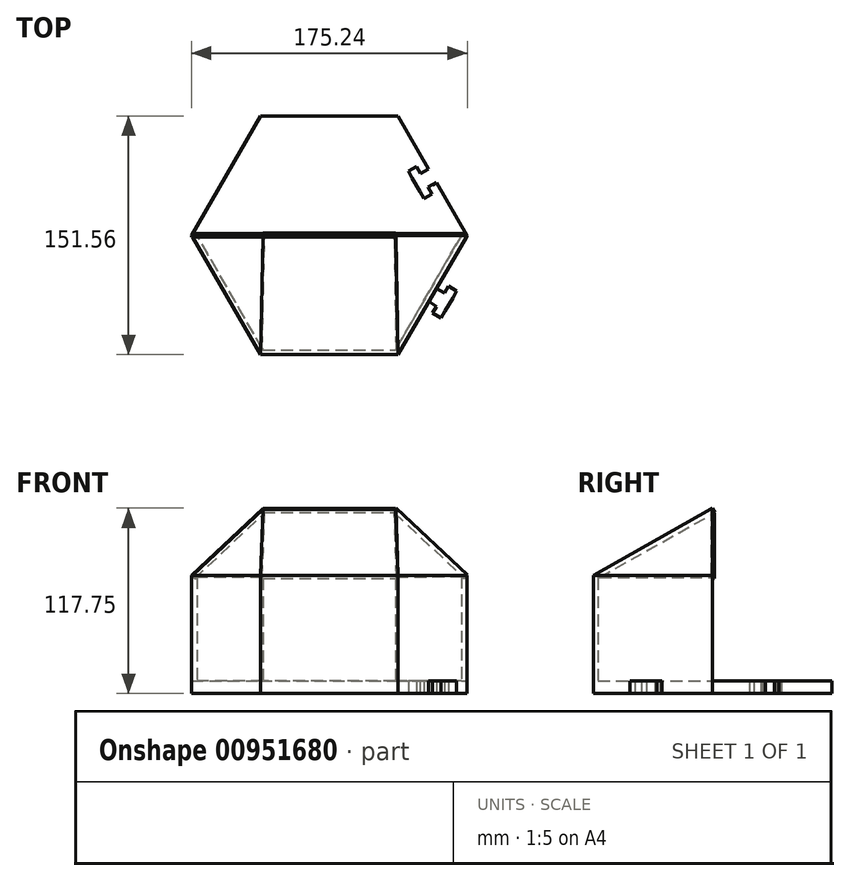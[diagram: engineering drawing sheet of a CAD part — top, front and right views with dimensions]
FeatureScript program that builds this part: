
annotation { "Feature Type Name" : "Feature", "Feature Type Description" : "" }
export const myFeature = defineFeature(function(context is Context, id is Id, definition is map)
    precondition{}
    {
        {
            var Q0;
            Q0=qCreatedBy(makeId("Top.planeOp"),FACE);
            var sketch = newSketch(context, id + "F0", { "sketchPlane" : qUnion([Q0])});
            skCircle(sketch, "E0.cCircle", {"center": v(0, 0) * mm, "radius": 75.78 * mm, "construction": true});
            skLineSegment(sketch, "E0.0", {"start": v(-43.75, 75.78) * mm, "end": v(43.75, 75.78) * mm});
            skLineSegment(sketch, "E0.1", {"start": v(43.75, 75.78) * mm, "end": v(87.5, 0) * mm});
            skLineSegment(sketch, "E0.2", {"start": v(87.5, 0) * mm, "end": v(43.75, -75.78) * mm});
            skLineSegment(sketch, "E0.3", {"start": v(43.75, -75.78) * mm, "end": v(-43.75, -75.78) * mm});
            skLineSegment(sketch, "E0.4", {"start": v(-43.75, -75.78) * mm, "end": v(-87.5, 0) * mm});
            skLineSegment(sketch, "E0.5", {"start": v(-87.5, 0) * mm, "end": v(-43.75, 75.78) * mm});
            skPoint(sketch, "E0.0.midPoint", {"position": v(0, 75.78) * mm});
            skLineSegment(sketch, "E1.0", {"start": v(-84.04, 0) * mm, "end": v(-42.02, 72.78) * mm});
            skLineSegment(sketch, "E1.1", {"start": v(42.02, 72.78) * mm, "end": v(84.04, 0) * mm});
            skLineSegment(sketch, "E1.2", {"start": v(84.04, 0) * mm, "end": v(42.02, -72.78) * mm});
            skLineSegment(sketch, "E1.3", {"start": v(-42.02, 72.78) * mm, "end": v(42.02, 72.78) * mm});
            skLineSegment(sketch, "E1.4", {"start": v(42.02, -72.78) * mm, "end": v(-42.02, -72.78) * mm});
            skLineSegment(sketch, "E1.5", {"start": v(-42.02, -72.78) * mm, "end": v(-84.04, 0) * mm});
            skLineSegment(sketch, "E2", {"start": v(-87.5, 0) * mm, "end": v(-84.04, 0) * mm});
            skLineSegment(sketch, "E3", {"start": v(84.04, 0) * mm, "end": v(87.5, 0) * mm});
            skLineSegment(sketch, "E4", {"start": v(0, 0) * mm, "end": v(0, 72.78) * mm, "construction": true});
            skLineSegment(sketch, "E5", {"start": v(0, 0) * mm, "end": v(42.02, 72.78) * mm, "construction": true});
            skLineSegment(sketch, "E6", {"start": v(0, 0) * mm, "end": v(-42.02, 72.78) * mm, "construction": true});
            skLineSegment(sketch, "E7", {"start": v(0, 36.39) * mm, "end": v(0, 72.78) * mm, "construction": true});
            skLineSegment(sketch, "E8.bottom", {"start": v(25, 48.33) * mm, "end": v(-25, 48.33) * mm});
            skLineSegment(sketch, "E8.top", {"start": v(25, 60.83) * mm, "end": v(-25, 60.83) * mm});
            skLineSegment(sketch, "E8.left", {"start": v(25, 48.33) * mm, "end": v(25, 60.83) * mm});
            skLineSegment(sketch, "E8.right", {"start": v(-25, 48.33) * mm, "end": v(-25, 60.83) * mm});
            skPoint(sketch, "E8.middle", {"position": v(0, 54.58) * mm});
            skLineSegment(sketch, "E9", {"start": v(-55.16, 32) * mm, "end": v(-52.71, 36.37) * mm, "construction": true});
            skLineSegment(sketch, "E10", {"start": v(-65.63, 37.89) * mm, "end": v(-68.13, 33.56) * mm});
            skLineSegment(sketch, "E11.MirrorCS", {"start": v(55.16, 32) * mm, "end": v(57.62, 27.65) * mm});
            skLineSegment(sketch, "E12.MirrorCS", {"start": v(55.16, 32) * mm, "end": v(52.71, 36.37) * mm});
            skLineSegment(sketch, "E13.MirrorCS", {"start": v(57.62, 27.65) * mm, "end": v(68.13, 33.56) * mm});
            skLineSegment(sketch, "E14.MirrorCS", {"start": v(87.5, 0) * mm, "end": v(43.75, 75.78) * mm});
            skLineSegment(sketch, "E15.MirrorCS", {"start": v(52.71, 36.37) * mm, "end": v(63.12, 42.22) * mm});
            skLineSegment(sketch, "E16.MirrorCS", {"start": v(57.97, 39.32) * mm, "end": v(55.52, 43.68) * mm});
            skLineSegment(sketch, "E17.MirrorCS", {"start": v(55.52, 43.68) * mm, "end": v(50.26, 40.72) * mm});
            skLineSegment(sketch, "E18.MirrorCS", {"start": v(52.71, 36.37) * mm, "end": v(50.26, 40.72) * mm});
            skLineSegment(sketch, "E19.MirrorCS", {"start": v(57.62, 27.65) * mm, "end": v(60.07, 23.3) * mm});
            skLineSegment(sketch, "E20.MirrorCS", {"start": v(62.87, 30.6) * mm, "end": v(65.32, 26.25) * mm});
            skLineSegment(sketch, "E21.MirrorCS", {"start": v(65.32, 26.25) * mm, "end": v(60.07, 23.3) * mm});
            skPoint(sketch, "E22.endSnap0", {"position": v(-68.26, -45.15) * mm});
            skLineSegment(sketch, "E23.MirrorCS", {"start": v(68.26, -45.15) * mm, "end": v(65.74, -49.4) * mm});
            skLineSegment(sketch, "E24.MirrorCS", {"start": v(65.74, -49.4) * mm, "end": v(70.88, -52.4) * mm});
            skLineSegment(sketch, "E25.MirrorCS", {"start": v(73.4, -48.2) * mm, "end": v(70.88, -52.4) * mm});
            skLineSegment(sketch, "E26.MirrorCS", {"start": v(73.4, -48.2) * mm, "end": v(63.12, -42.1) * mm});
            skLineSegment(sketch, "E27.MirrorCS", {"start": v(78.45, -39.68) * mm, "end": v(73.4, -48.2) * mm});
            skLineSegment(sketch, "E28.MirrorCS", {"start": v(78.45, -39.68) * mm, "end": v(68.12, -33.56) * mm});
            skLineSegment(sketch, "E29.MirrorCS", {"start": v(73.33, -36.65) * mm, "end": v(75.88, -32.34) * mm});
            skLineSegment(sketch, "E30.MirrorCS", {"start": v(75.88, -32.34) * mm, "end": v(80.95, -35.46) * mm});
            skLineSegment(sketch, "E31.MirrorCS", {"start": v(78.45, -39.68) * mm, "end": v(81, -35.38) * mm});
            skLineSegment(sketch, "E32", {"start": v(68.13, 33.56) * mm, "end": v(65.53, 32.06) * mm});
            skSolve(sketch);
        }
        {
            var Q0;
            Q0=makeQuery(id+"F0.imprint","IMPRINT",FACE,{"disambiguationData":[TD([[makeQuery(id+"F0.imprint","IMPRINT",EDGE,{"derivedFrom":sQuery(id+"F0.wireOp",EDGE,"E1.0")}),-1.0]])]});
            extrude(context, id + "F1", {"entities" : qUnion([Q0]), "depth" : 8 * mm, "offsetDistance" : 25 * mm});
        }
        {
            var Q0;
            Q0=makeQuery(id+"F0.imprint","IMPRINT",FACE,{"disambiguationData":[TD([[makeQuery(id+"F0.imprint","IMPRINT",EDGE,{"derivedFrom":sQuery(id+"F0.wireOp",EDGE,"E0.2")}),-1.0]])]});
            extrude(context, id + "F2", {"entities" : qUnion([Q0]), "operationType" : NewBodyOperationType.ADD, "depth" : 75 * mm, "offsetDistance" : 25 * mm});
        }
        {
            var Q0;
            Q0=qCreatedBy(makeId("Front.planeOp"),FACE);
            var sketch = newSketch(context, id + "F3", { "sketchPlane" : qUnion([Q0])});
            skLineSegment(sketch, "E33", {"start": v(0, 0) * mm, "end": v(0, 144.27) * mm, "construction": true});
            skLineSegment(sketch, "E34", {"start": v(0, 144.27) * mm, "end": v(-94, 144.27) * mm, "construction": true});
            skLineSegment(sketch, "E35", {"start": v(0, 144.27) * mm, "end": v(81.74, 144.27) * mm});
            skLineSegment(sketch, "E36", {"start": v(0, 0) * mm, "end": v(0, 75) * mm, "construction": true});
            skLineSegment(sketch, "E37", {"start": v(0, 75) * mm, "end": v(0, 114.5) * mm, "construction": true});
            skLineSegment(sketch, "E38", {"start": v(0, 75) * mm, "end": v(-87.5, 75) * mm, "construction": true});
            skLineSegment(sketch, "E39", {"start": v(0, 114.5) * mm, "end": v(42.02, 114.5) * mm, "construction": true});
            skLineSegment(sketch, "E40", {"start": v(0, 114.5) * mm, "end": v(-42.02, 114.5) * mm});
            skLineSegment(sketch, "E41", {"start": v(0, 75) * mm, "end": v(-84.04, 75) * mm, "construction": true});
            skLineSegment(sketch, "E42", {"start": v(-42.02, 114.5) * mm, "end": v(-84.04, 75) * mm});
            skLineSegment(sketch, "E43", {"start": v(-42.02, 114.5) * mm, "end": v(-42.02, 117.5) * mm, "construction": true});
            skLineSegment(sketch, "E44", {"start": v(-42.02, 117.5) * mm, "end": v(-87.5, 75) * mm});
            skLineSegment(sketch, "E45", {"start": v(-42.02, 117.5) * mm, "end": v(0, 117.5) * mm});
            skLineSegment(sketch, "E46.MirrorCS", {"start": v(42.02, 117.5) * mm, "end": v(87.5, 75) * mm});
            skLineSegment(sketch, "E47.MirrorCS", {"start": v(42.02, 114.5) * mm, "end": v(84.04, 75) * mm});
            skLineSegment(sketch, "E48.MirrorCS", {"start": v(42.02, 117.5) * mm, "end": v(0, 117.5) * mm});
            skLineSegment(sketch, "E49.MirrorCS", {"start": v(0, 114.5) * mm, "end": v(42.02, 114.5) * mm});
            skLineSegment(sketch, "E50", {"start": v(87.5, 75) * mm, "end": v(84.04, 75) * mm});
            skLineSegment(sketch, "E51", {"start": v(-84.04, 75) * mm, "end": v(-87.5, 75) * mm});
            skSolve(sketch);
        }
        {
            var Q0;
            Q0=makeQuery(id+"F0.imprint","IMPRINT",FACE,{"disambiguationData":[TD([[makeQuery(id+"F0.imprint","IMPRINT",EDGE,{"derivedFrom":sQuery(id+"F0.wireOp",EDGE,"E0.0")}),-1.0]])]});
            extrude(context, id + "F4", {"entities" : qUnion([Q0]), "operationType" : NewBodyOperationType.ADD, "oppositeDirection" : true, "depth" : -8 * mm, "offsetDistance" : 25 * mm});
        }
        {
            var Q0;
            Q0=makeQuery(id+"F2.opExtrude","CAP_EDGE",EDGE,{"disambiguationData":[OSD([sQuery(id+"F0.wireOp",EDGE,"E0.3")])],"isStart":false});
            var Q1;
            Q1=sQuery(id+"F3.wireOp",VERTEX,"E45.end");
            cPlane(context, id + "F5", {"entities" : qUnion([Q0, Q1]), "cplaneType" : CPlaneType.LINE_ANGLE, "offset" : 25 * mm, "angle" : 0 * degree, "width" : 150 * mm, "height" : 150 * mm});
        }
        {
            var Q0;
            Q0=qCreatedBy(id+"F5.planeOp",FACE);
            var sketch = newSketch(context, id + "F6", { "sketchPlane" : qUnion([Q0])});
            skLineSegment(sketch, "E52", {"start": v(0, 29.4) * mm, "end": v(43.75, 29.4) * mm});
            skLineSegment(sketch, "E53", {"start": v(0, 29.4) * mm, "end": v(-43.75, 29.4) * mm});
            skLineSegment(sketch, "E54", {"start": v(-43.75, 29.4) * mm, "end": v(-42.02, -57.48) * mm});
            skLineSegment(sketch, "E55", {"start": v(43.75, 29.4) * mm, "end": v(42.02, -57.48) * mm});
            skLineSegment(sketch, "E56", {"start": v(-42.02, -57.48) * mm, "end": v(42.02, -57.48) * mm});
            skSolve(sketch);
        }
        {
            var Q0;
            Q0=makeQuery(id+"F6.imprint","IMPRINT",FACE,{"disambiguationData":[TD([[makeQuery(id+"F6.imprint","IMPRINT",EDGE,{"derivedFrom":sQuery(id+"F6.wireOp",EDGE,"E52")}),-1.0]])]});
            extrude(context, id + "F7", {"entities" : qUnion([Q0]), "operationType" : NewBodyOperationType.ADD, "depth" : 3 * mm, "offsetDistance" : 25 * mm});
        }
        {
            var Q0;
            Q0=makeQuery(id+"F3.imprint","IMPRINT",FACE,{"disambiguationData":[TD([[makeQuery(id+"F3.imprint","IMPRINT",EDGE,{"derivedFrom":sQuery(id+"F3.wireOp",EDGE,"E40")}),-1.0]])]});
            extrude(context, id + "F8", {"entities" : qUnion([Q0]), "operationType" : NewBodyOperationType.ADD, "depth" : 1 * mm, "offsetDistance" : 25 * mm});
        }
        {
            var Q0;
            Q0=makeQuery(id+"F8.opExtrude","CAP_EDGE",EDGE,{"disambiguationData":[OSD([sQuery(id+"F3.wireOp",EDGE,"E44")])],"isStart":true});
            var Q1;
            Q1=makeQuery(id+"F7.boolean.opBoolean","MERGE",VERTEX,{"derivedFrom":[makeQuery(id+"F2.opExtrude","CAP_VERTEX",VERTEX,{"disambiguationData":[OSD([sQuery(id+"F0.wireOp",EDGE,"E0.3"),sQuery(id+"F0.wireOp",EDGE,"E0.4")])],"isStart":false}),makeQuery(id+"F7.opExtrude","CAP_VERTEX",VERTEX,{"disambiguationData":[OSD([sQuery(id+"F6.wireOp",EDGE,"E53"),sQuery(id+"F6.wireOp",EDGE,"E54")])],"isStart":true})]});
            cPlane(context, id + "F9", {"entities" : qUnion([Q0, Q1]), "cplaneType" : CPlaneType.LINE_ANGLE, "offset" : 25 * mm, "angle" : 0 * degree, "width" : 150 * mm, "height" : 150 * mm});
        }
        {
            var Q0;
            Q0=qCreatedBy(id+"F9.planeOp",FACE);
            var sketch = newSketch(context, id + "F10", { "sketchPlane" : qUnion([Q0])});
            skLineSegment(sketch, "E57", {"start": v(-25.66, 35.61) * mm, "end": v(30.99, -31.08) * mm});
            skLineSegment(sketch, "E58", {"start": v(-25.66, 35.61) * mm, "end": v(33.23, 55.79) * mm});
            skLineSegment(sketch, "E59", {"start": v(33.23, 55.79) * mm, "end": v(30.99, -31.08) * mm});
            skSolve(sketch);
        }
        {
            var Q0;
            Q0=qSketchRegion(id+"F10",true);
            extrude(context, id + "F11", {"entities" : qUnion([Q0]), "operationType" : NewBodyOperationType.ADD, "depth" : -3 * mm, "offsetDistance" : 25 * mm});
        }
        {
            var Q0;
            Q0=makeQuery(id+"F8.opExtrude","CAP_EDGE",EDGE,{"disambiguationData":[OSD([sQuery(id+"F3.wireOp",EDGE,"E46.MirrorCS")])],"isStart":false});
            var Q1;
            Q1=makeQuery(id+"F7.boolean.opBoolean","MERGE",VERTEX,{"derivedFrom":[makeQuery(id+"F2.opExtrude","CAP_VERTEX",VERTEX,{"disambiguationData":[OSD([sQuery(id+"F0.wireOp",EDGE,"E0.2"),sQuery(id+"F0.wireOp",EDGE,"E0.3")])],"isStart":false}),makeQuery(id+"F7.opExtrude","CAP_VERTEX",VERTEX,{"disambiguationData":[OSD([sQuery(id+"F6.wireOp",EDGE,"E52"),sQuery(id+"F6.wireOp",EDGE,"E55")])],"isStart":true})]});
            cPlane(context, id + "F12", {"entities" : qUnion([Q0, Q1]), "cplaneType" : CPlaneType.LINE_ANGLE, "offset" : 25 * mm, "angle" : 0 * degree, "width" : 150 * mm, "height" : 150 * mm});
        }
        {
            var Q0;
            Q0=qCreatedBy(id+"F12.planeOp",FACE);
            var sketch = newSketch(context, id + "F13", { "sketchPlane" : qUnion([Q0])});
            skLineSegment(sketch, "E60", {"start": v(-32.88, -56.36) * mm, "end": v(25.94, -35.98) * mm});
            skLineSegment(sketch, "E61", {"start": v(25.94, -35.98) * mm, "end": v(-30.94, 30.51) * mm});
            skLineSegment(sketch, "E62", {"start": v(-30.94, 30.51) * mm, "end": v(-32.88, -56.36) * mm});
            skSolve(sketch);
        }
        {
            var Q0;
            Q0=qSketchRegion(id+"F13",true);
            extrude(context, id + "F14", {"entities" : qUnion([Q0]), "operationType" : NewBodyOperationType.ADD, "depth" : 3 * mm, "offsetDistance" : 25 * mm});
        }
        {
            var Q0;
            Q0=makeQuery(id+"F0.imprint","IMPRINT",FACE,{"disambiguationData":[TD([[makeQuery(id+"F0.imprint","IMPRINT",EDGE,{"derivedFrom":sQuery(id+"F0.wireOp",EDGE,"E8.bottom")}),-1.0]])]});
            extrude(context, id + "F15", {"entities" : qUnion([Q0]), "operationType" : NewBodyOperationType.ADD, "depth" : 8 * mm, "offsetDistance" : 25 * mm});
        }
        {
            var Q0;
            {var subQ5=sQuery(id+"F0.wireOp",EDGE,"749d55a2-1ae5-4b90-8efe-ab6072e4ac770.MirrorCS");Q0=makeQuery(id+"F0.imprint","IMPRINT",FACE,{"disambiguationData":[TD([[makeQuery(id+"F0.imprint","IMPRINT",EDGE,{"derivedFrom":subQ5}),1.0]])]});}
            var Q1;
            {var subQ4=sQuery(id+"F0.wireOp",EDGE,"bf9a6782-c77d-4324-b6f4-6efb0bd9360c0.MirrorCS");Q1=makeQuery(id+"F0.imprint","IMPRINT",FACE,{"disambiguationData":[TD([[makeQuery(id+"F0.imprint","IMPRINT",EDGE,{"derivedFrom":subQ4}),1.0]])]});}
            var Q2;
            {var subQ0=sQuery(id+"F0.wireOp",EDGE,"c1ebaf2c-39ee-4834-980c-edcd090fc9720.MirrorCS");Q2=makeQuery(id+"F0.imprint","IMPRINT",FACE,{"disambiguationData":[TD([[makeQuery(id+"F0.imprint","IMPRINT",EDGE,{"derivedFrom":subQ0}),1.0]])]});}
            var Q3;
            {var subQ5=sQuery(id+"F0.wireOp",EDGE,"E30.MirrorCS");Q3=makeQuery(id+"F0.imprint","IMPRINT",FACE,{"disambiguationData":[TD([[makeQuery(id+"F0.imprint","IMPRINT",EDGE,{"derivedFrom":subQ5}),-1.0]])]});}
            var Q4;
            {var subQ0=sQuery(id+"F0.wireOp",EDGE,"E27.MirrorCS");Q4=makeQuery(id+"F0.imprint","IMPRINT",FACE,{"disambiguationData":[TD([[makeQuery(id+"F0.imprint","IMPRINT",EDGE,{"derivedFrom":subQ0}),-1.0]])]});}
            var Q5;
            {var subQ0=sQuery(id+"F0.wireOp",EDGE,"E23.MirrorCS");Q5=makeQuery(id+"F0.imprint","IMPRINT",FACE,{"disambiguationData":[TD([[makeQuery(id+"F0.imprint","IMPRINT",EDGE,{"derivedFrom":subQ0}),1.0]])]});}
            extrude(context, id + "F16", {"entities" : qUnion([Q0, Q1, Q2, Q3, Q4, Q5]), "operationType" : NewBodyOperationType.ADD, "depth" : 8 * mm, "offsetDistance" : 25 * mm});
        }
        {
            var Q0;
            {var subQ0=sQuery(id+"F0.wireOp",EDGE,"E3");Q0=makeQuery(id+"F0.imprint","IMPRINT",FACE,{"disambiguationData":[TD([[makeQuery(id+"F0.imprint","IMPRINT",EDGE,{"derivedFrom":subQ0}),1.0]])]});}
            extrude(context, id + "F17", {"entities" : qUnion([Q0]), "operationType" : NewBodyOperationType.ADD, "depth" : 8 * mm, "offsetDistance" : 25 * mm});
        }
    });
